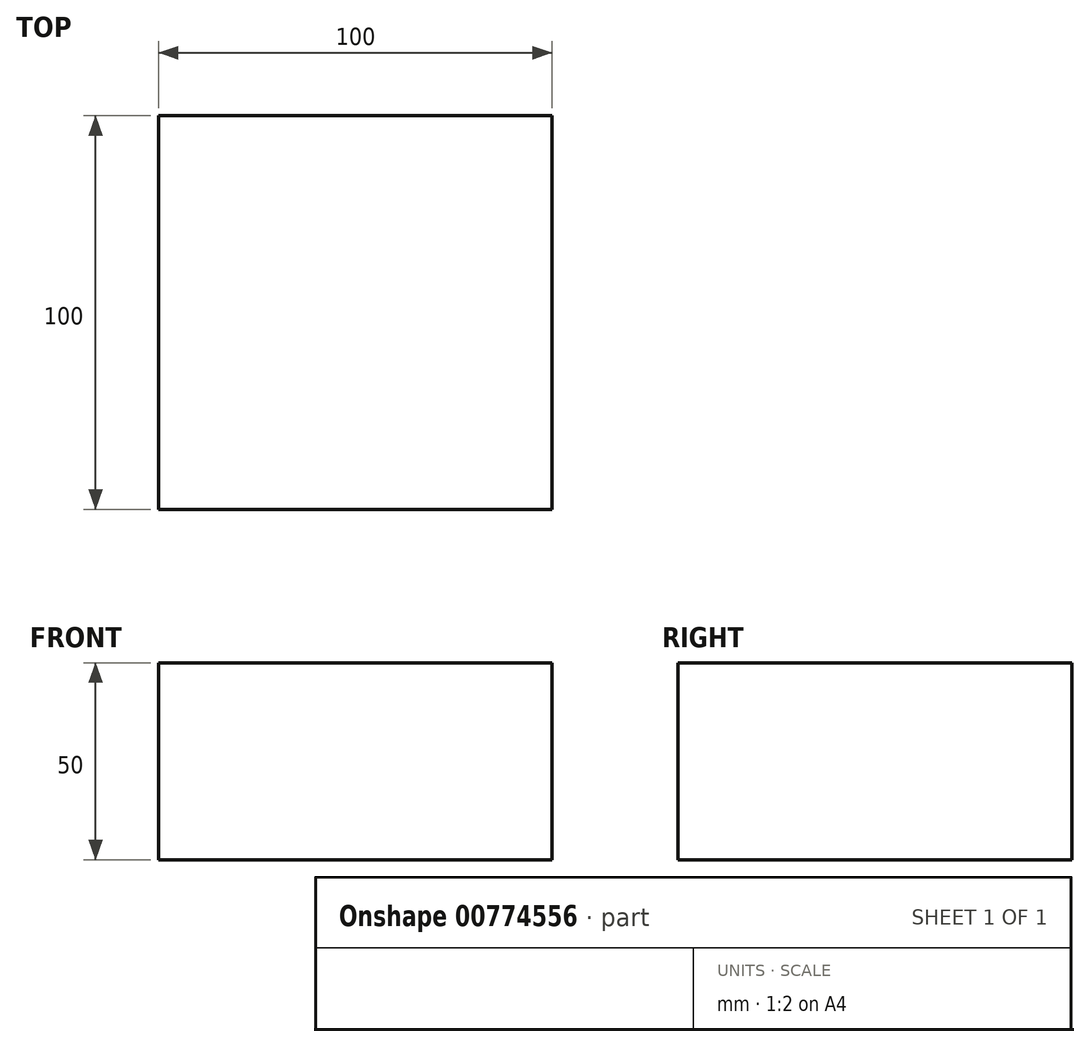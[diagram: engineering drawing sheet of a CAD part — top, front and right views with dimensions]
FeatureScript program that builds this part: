
annotation { "Feature Type Name" : "Feature", "Feature Type Description" : "" }
export const myFeature = defineFeature(function(context is Context, id is Id, definition is map)
    precondition{}
    {
        {
            var Q0;
            Q0=qCreatedBy(makeId("Top.planeOp"),FACE);
            var sketch = newSketch(context, id + "F0", { "sketchPlane" : qUnion([Q0])});
            skLineSegment(sketch, "E0.bottom", {"start": v(50, -50) * mm, "end": v(-50, -50) * mm});
            skLineSegment(sketch, "E0.top", {"start": v(50, 50) * mm, "end": v(-50, 50) * mm});
            skLineSegment(sketch, "E0.left", {"start": v(50, -50) * mm, "end": v(50, 50) * mm});
            skLineSegment(sketch, "E0.right", {"start": v(-50, -50) * mm, "end": v(-50, 50) * mm});
            skPoint(sketch, "E0.middle", {"position": v(0, 0) * mm});
            skSolve(sketch);
        }
        {
            var Q0;
            Q0 = qSketchRegion(id + "F0", true);
            extrude(context, id + "F1", {"entities" : qUnion([Q0]), "depth" : 50 * mm, "offsetDistance" : 25 * mm});
        }
    });
